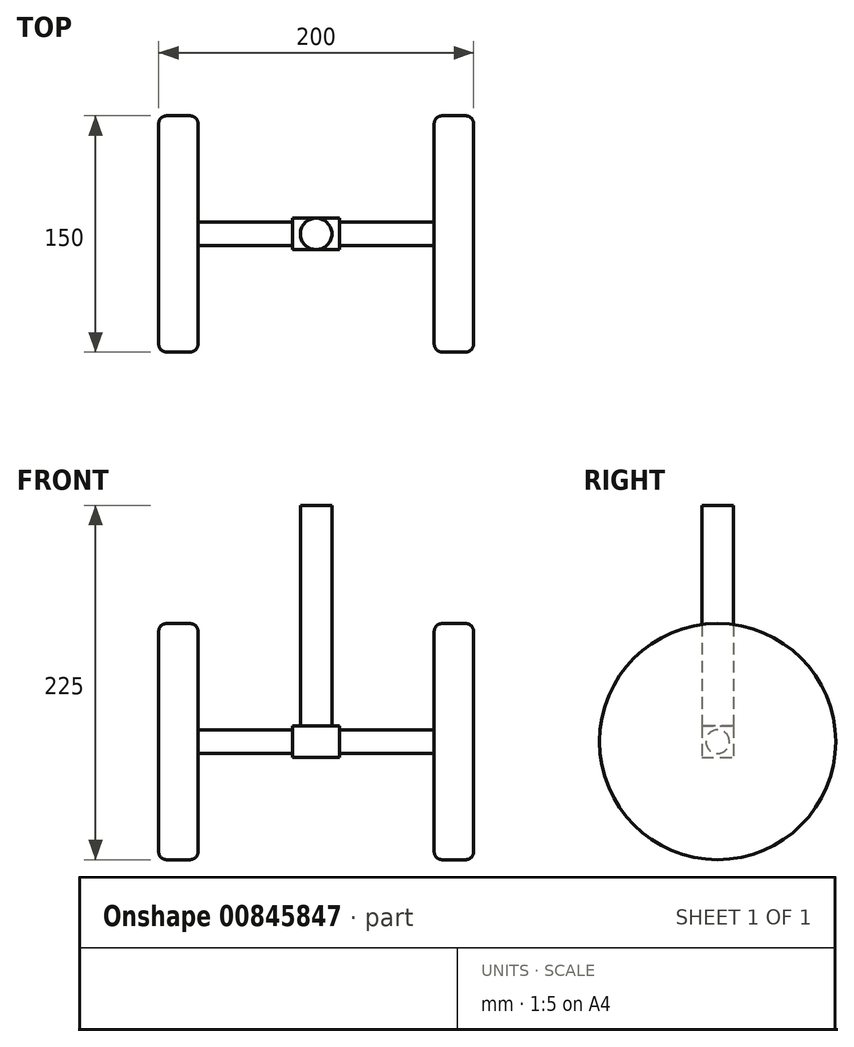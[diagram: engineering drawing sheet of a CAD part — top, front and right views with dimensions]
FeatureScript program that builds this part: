
annotation { "Feature Type Name" : "Feature", "Feature Type Description" : "" }
export const myFeature = defineFeature(function(context is Context, id is Id, definition is map)
    precondition{}
    {
        {
            var Q0;
            Q0=qCreatedBy(makeId("Front.planeOp"),FACE);
            var sketch = newSketch(context, id + "F0", { "sketchPlane" : qUnion([Q0])});
            skLineSegment(sketch, "E0.bottom", {"start": v(-15, 10) * mm, "end": v(15, 10) * mm});
            skLineSegment(sketch, "E0.top", {"start": v(-15, -10) * mm, "end": v(15, -10) * mm});
            skLineSegment(sketch, "E0.left", {"start": v(-15, 10) * mm, "end": v(-15, -10) * mm});
            skLineSegment(sketch, "E0.right", {"start": v(15, 10) * mm, "end": v(15, -10) * mm});
            skSolve(sketch);
        }
        {
            var Q0;
            Q0 = qSketchRegion(id + "F0", true);
            extrude(context, id + "F1", {"entities" : qUnion([Q0]), "depth" : 10 * mm, "offsetDistance" : 25 * mm, "hasSecondDirection" : true, "secondDirectionOppositeDirection" : true, "secondDirectionDepth" : 10 * mm});
        }
        {
            var Q0;
            Q0=qCreatedBy(makeId("Right.planeOp"),FACE);
            var sketch = newSketch(context, id + "F2", { "sketchPlane" : qUnion([Q0])});
            skCircle(sketch, "E1", {"center": v(0, 0) * mm, "radius": 7.5 * mm});
            skSolve(sketch);
        }
        {
            var Q0;
            Q0 = qSketchRegion(id + "F2", true);
            extrude(context, id + "F3", {"entities" : qUnion([Q0]), "operationType" : NewBodyOperationType.ADD, "depth" : 75 * mm, "offsetDistance" : 25 * mm, "hasSecondDirection" : true, "secondDirectionOppositeDirection" : true, "secondDirectionDepth" : 75 * mm});
        }
        {
            var Q0;
            Q0=makeQuery(id+"F3.opExtrude","CAP_FACE",FACE,{"disambiguationData":[OSD([sQuery(id+"F2.wireOp",EDGE,"E1")])],"isStart":false});
            var sketch = newSketch(context, id + "F4", { "sketchPlane" : qUnion([Q0])});
            skCircle(sketch, "E2", {"center": v(0, 0) * mm, "radius": 75 * mm});
            skSolve(sketch);
        }
        {
            var Q0;
            Q0 = qSketchRegion(id + "F4", true);
            extrude(context, id + "F5", {"entities" : qUnion([Q0]), "depth" : 25 * mm, "offsetDistance" : 25 * mm});
        }
        {
            var Q0;
            Q0=makeQuery(id+"F5.opExtrude","CAP_EDGE",EDGE,{"disambiguationData":[OSD([sQuery(id+"F4.wireOp",EDGE,"E2")])],"isStart":true});
            var Q1;
            Q1=makeQuery(id+"F5.opExtrude","CAP_FACE",FACE,{"disambiguationData":[OSD([sQuery(id+"F4.wireOp",EDGE,"E2")])],"isStart":false});
            fillet(context, id + "F6", {"entities" : qUnion([Q0, Q1]), "radius" : 5 * mm, "tangentPropagation" : true, "allowEdgeOverflow" : false});
        }
        {
            var Q0;
            Q0=makeQuery(id+"F3.opExtrude","CAP_FACE",FACE,{"disambiguationData":[OSD([sQuery(id+"F2.wireOp",EDGE,"E1")])],"isStart":true});
            var sketch = newSketch(context, id + "F7", { "sketchPlane" : qUnion([Q0])});
            skCircle(sketch, "E3", {"center": v(0, 0) * mm, "radius": 75 * mm});
            skSolve(sketch);
        }
        {
            var Q0;
            Q0 = qSketchRegion(id + "F7", true);
            extrude(context, id + "F8", {"entities" : qUnion([Q0]), "operationType" : NewBodyOperationType.ADD, "depth" : 25 * mm, "offsetDistance" : 25 * mm});
        }
        {
            var Q0;
            Q0=makeQuery(id+"F8.opExtrude","CAP_EDGE",EDGE,{"disambiguationData":[OSD([sQuery(id+"F7.wireOp",EDGE,"E3")])],"isStart":false});
            var Q1;
            Q1=makeQuery(id+"F8.opExtrude","CAP_EDGE",EDGE,{"disambiguationData":[OSD([sQuery(id+"F7.wireOp",EDGE,"E3")])],"isStart":true});
            fillet(context, id + "F9", {"entities" : qUnion([Q0, Q1]), "radius" : 5 * mm, "tangentPropagation" : true, "allowEdgeOverflow" : false});
        }
        {
            var Q0;
            Q0=qCreatedBy(makeId("Top.planeOp"),FACE);
            var sketch = newSketch(context, id + "F10", { "sketchPlane" : qUnion([Q0])});
            skCircle(sketch, "E4", {"center": v(0, 0) * mm, "radius": 10 * mm});
            skSolve(sketch);
        }
        {
            var Q0;
            Q0 = qSketchRegion(id + "F10", true);
            extrude(context, id + "F11", {"entities" : qUnion([Q0]), "operationType" : NewBodyOperationType.ADD, "depth" : 150 * mm, "offsetDistance" : 25 * mm});
        }
    });
